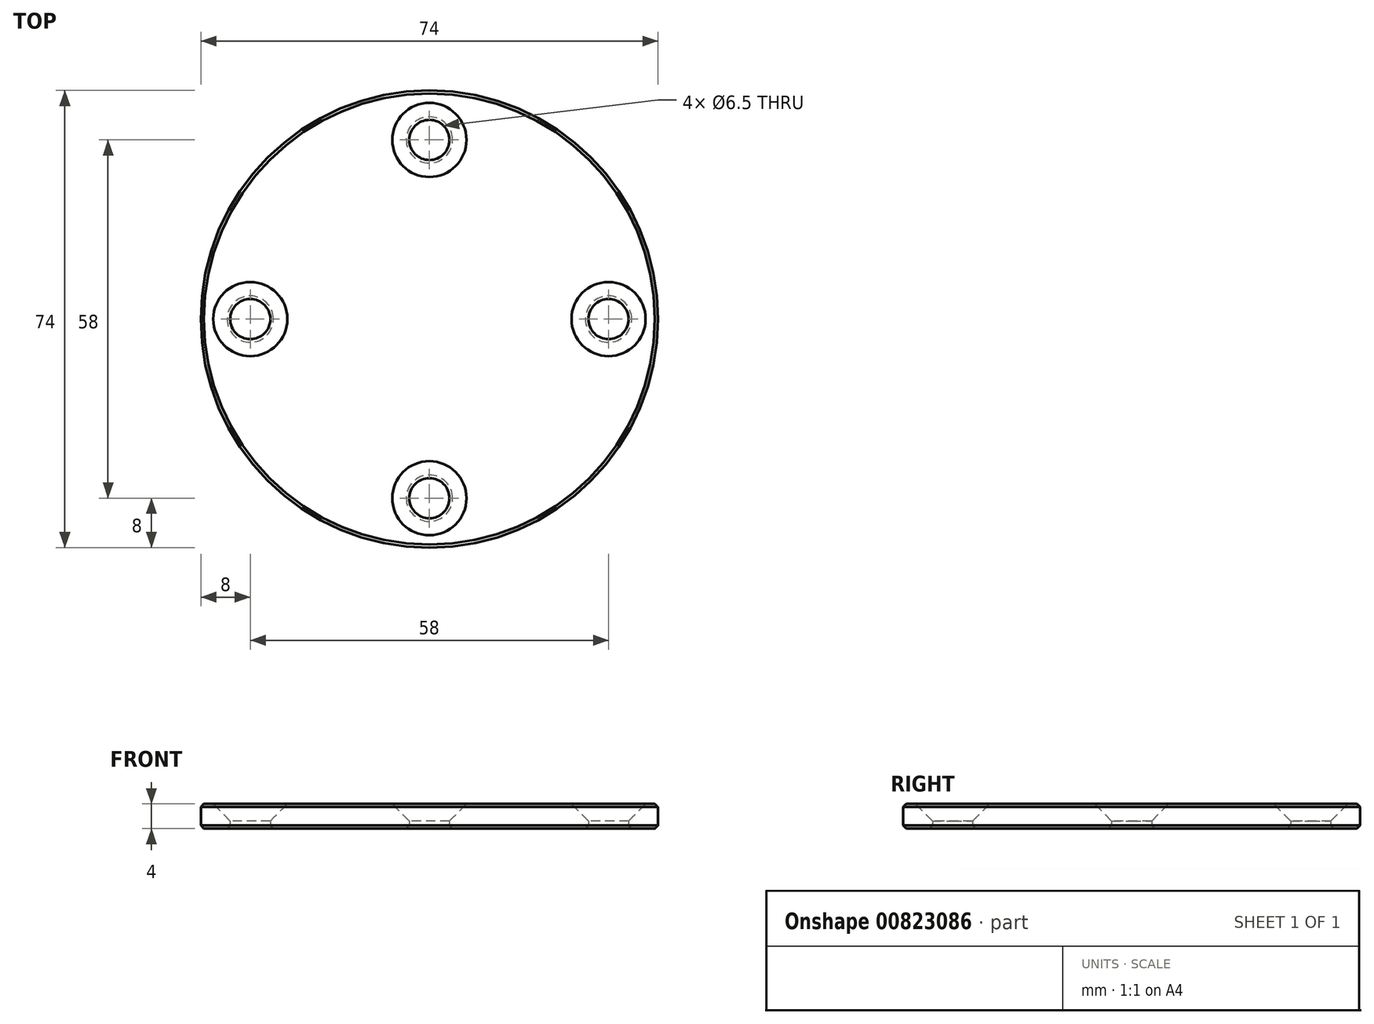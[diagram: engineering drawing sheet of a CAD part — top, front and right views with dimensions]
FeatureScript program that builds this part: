
annotation { "Feature Type Name" : "Feature", "Feature Type Description" : "" }
export const myFeature = defineFeature(function(context is Context, id is Id, definition is map)
    precondition{}
    {
        {
            var Q0;
            Q0=qCreatedBy(makeId("Top.planeOp"),FACE);
            var sketch = newSketch(context, id + "F0", { "sketchPlane" : qUnion([Q0])});
            skCircle(sketch, "E0", {"center": v(0, 0) * mm, "radius": 16 * mm, "construction": true});
            skCircle(sketch, "E1", {"center": v(0, 0) * mm, "radius": 29 * mm, "construction": true});
            skCircle(sketch, "E2", {"center": v(0, 0) * mm, "radius": 37 * mm});
            skLineSegment(sketch, "E3", {"start": v(0, -37) * mm, "end": v(0, 37) * mm, "construction": true});
            skLineSegment(sketch, "E4", {"start": v(0, 37) * mm, "end": v(37, 0) * mm, "construction": true});
            skLineSegment(sketch, "E5", {"start": v(37, 0) * mm, "end": v(-37, 0) * mm, "construction": true});
            skCircle(sketch, "E6", {"center": v(0, 29) * mm, "radius": 3.25 * mm});
            skCircle(sketch, "E7", {"center": v(-29, 0) * mm, "radius": 3.25 * mm});
            skCircle(sketch, "E8", {"center": v(0, -29) * mm, "radius": 3.25 * mm});
            skCircle(sketch, "E9", {"center": v(29, 0) * mm, "radius": 3.25 * mm});
            skSolve(sketch);
        }
        {
            var Q0;
            Q0=qSketchRegion(id+"F0",true);
            extrude(context, id + "F1", {"entities" : qUnion([Q0]), "depth" : 4 * mm, "offsetDistance" : 25 * mm});
        }
        {
            var Q0;
            Q0=makeQuery(id+"F1.opExtrude","CAP_EDGE",EDGE,{"disambiguationData":[OSD([sQuery(id+"F0.wireOp",EDGE,"E8")])],"isStart":false});
            var Q1;
            Q1=makeQuery(id+"F1.opExtrude","CAP_EDGE",EDGE,{"disambiguationData":[OSD([sQuery(id+"F0.wireOp",EDGE,"E7")])],"isStart":false});
            var Q2;
            Q2=makeQuery(id+"F1.opExtrude","CAP_EDGE",EDGE,{"disambiguationData":[OSD([sQuery(id+"F0.wireOp",EDGE,"E6")])],"isStart":false});
            var Q3;
            Q3=makeQuery(id+"F1.opExtrude","CAP_EDGE",EDGE,{"disambiguationData":[OSD([sQuery(id+"F0.wireOp",EDGE,"E9")])],"isStart":false});
            chamfer(context, id + "F2", {"entities" : qUnion([Q0, Q1, Q2, Q3]), "width" : 2.75 * mm, "tangentPropagation" : true});
        }
        {
            var Q0;
            Q0=makeQuery(id+"F1.opExtrude","SWEPT_FACE",FACE,{"disambiguationData":[OSD([sQuery(id+"F0.wireOp",EDGE,"E2")])]});
            var Q1;
            Q1=makeQuery(id+"F1.opExtrude","CAP_EDGE",EDGE,{"disambiguationData":[OSD([sQuery(id+"F0.wireOp",EDGE,"E8")])],"isStart":true});
            var Q2;
            Q2=makeQuery(id+"F1.opExtrude","CAP_EDGE",EDGE,{"disambiguationData":[OSD([sQuery(id+"F0.wireOp",EDGE,"E7")])],"isStart":true});
            var Q3;
            Q3=makeQuery(id+"F1.opExtrude","CAP_EDGE",EDGE,{"disambiguationData":[OSD([sQuery(id+"F0.wireOp",EDGE,"E6")])],"isStart":true});
            var Q4;
            Q4=makeQuery(id+"F1.opExtrude","CAP_EDGE",EDGE,{"disambiguationData":[OSD([sQuery(id+"F0.wireOp",EDGE,"E9")])],"isStart":true});
            chamfer(context, id + "F3", {"entities" : qUnion([Q0, Q1, Q2, Q3, Q4]), "width" : 0.5 * mm, "tangentPropagation" : true});
        }
    });
